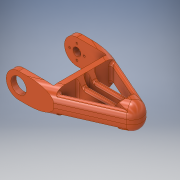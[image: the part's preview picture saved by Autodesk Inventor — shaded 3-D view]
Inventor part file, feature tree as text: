
AUTODESK INVENTOR PART (.ipt)
format: ipt  version: 2017 (Build 210142000, 142)  size: 521,216 bytes
history: native  units: mm
features: extrude x6, sketch x6, fillet x4
ambient origin geometry x8: Origin, YZ Plane, XZ Plane, XY Plane, X Axis, Y Axis, Z Axis, Center Point
bodies: Solid1 (feature_tree)
feature tree (16):
  extrude  "Extrusion1"  Depth=10.0mm
  extrude  "Extrusion8"  TaperAngle=0.0deg  [1 undecoded]
  extrude  "Extrusion9"  Depth=45.5mm
  fillet  "Fillet5"  Radius=5.0mm
  extrude  "Extrusion12"  Depth=5.0mm
  extrude  "Extrusion13"  Depth=10.0mm
  extrude  "Extrusion14"  Depth=10.0mm TaperAngle=0.0deg
  fillet  "Fillet7"  Radius=12.0mm
  fillet  "Fillet8"  Radius=15.0mm
  fillet  "Fillet9"  Radius=5.0mm
  sketch  "Sketch1"  dims[d0=90.0mm d1=10.0mm]
  sketch  "Sketch9"  dims[d2=24.0mm d3=0.0mm]
  sketch  "Sketch10"  dims[d4=61.0mm d68=45.5mm d69=5.0mm]
  sketch  "Sketch15"  dims[d70=5.0mm d71=5.0mm]
  sketch  "Sketch16"  dims[d72=10.0mm d73=0.0mm d74=5.0mm]
  sketch  "Sketch17"  dims[d75=5.0mm d77=10.0mm d78=0.0mm d80=12.0mm d81=15.0mm d82=5.0mm d95=15.0mm d96=10.0mm d97=0.0mm d98=7.7mm d99=2.0mm d100=7.0mm d101=7.0mm d102=7.0mm d103=7.0mm d104=10.0mm d105=0.0mm d106=60.0deg d107=60.0deg d108=60.0deg d109=60.0deg d110=10.0mm d111=10.0mm d112=0.0mm d113=10.0mm d115=2.0mm d116=1.0mm]
note: 1 required parameter value undecoded (feature->parameter linkage not recoverable at this tier; creation-order binding heuristic only, values carry confidence <= 0.55)
